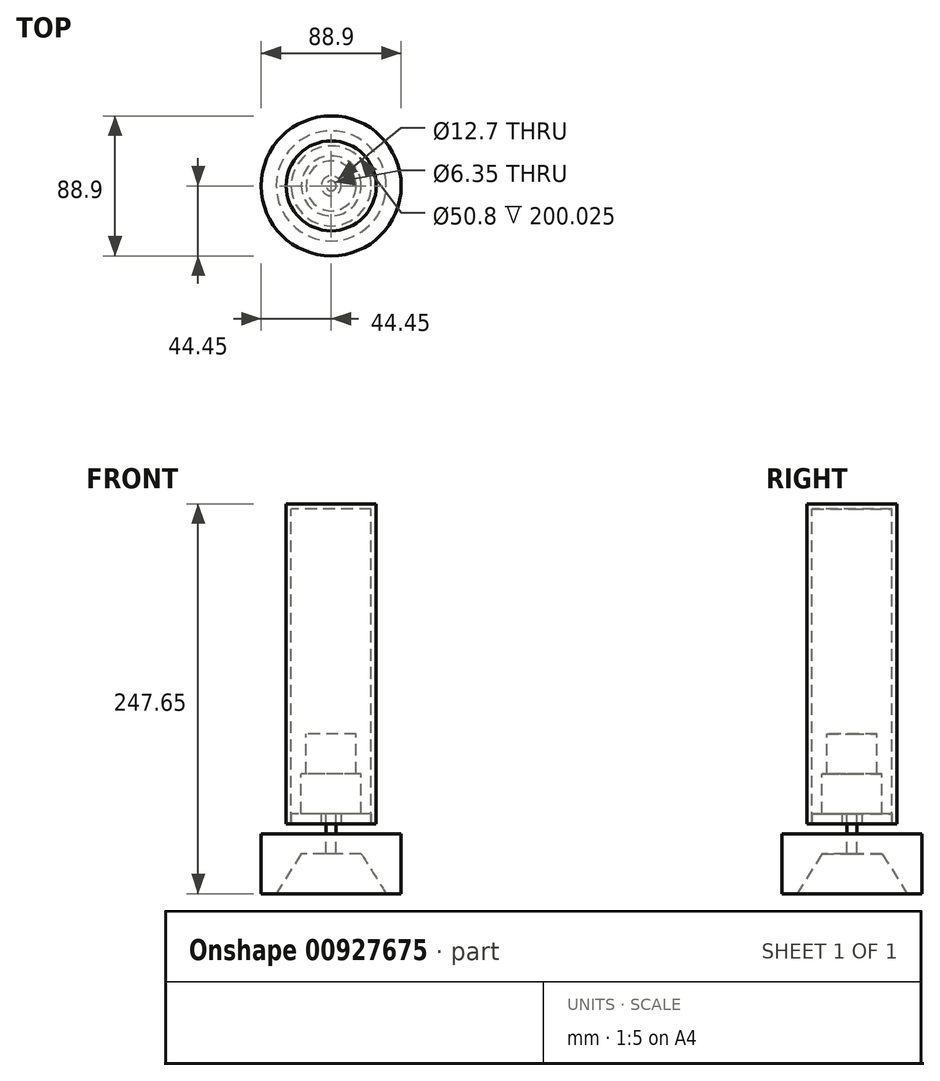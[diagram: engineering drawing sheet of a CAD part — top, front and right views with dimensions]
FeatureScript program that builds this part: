
annotation { "Feature Type Name" : "Feature", "Feature Type Description" : "" }
export const myFeature = defineFeature(function(context is Context, id is Id, definition is map)
    precondition{}
    {
        {
            var Q0;
            Q0=qCreatedBy(makeId("Front.planeOp"),FACE);
            var sketch = newSketch(context, id + "F0", { "sketchPlane" : qUnion([Q0])});
            skLineSegment(sketch, "E0", {"start": v(-25.4, 0) * mm, "end": v(-28.57, 0) * mm});
            skLineSegment(sketch, "E1", {"start": v(-28.57, 0) * mm, "end": v(-28.57, 203.2) * mm});
            skLineSegment(sketch, "E2", {"start": v(-28.57, 203.2) * mm, "end": v(0, 203.2) * mm});
            skLineSegment(sketch, "E3", {"start": v(0, 200.03) * mm, "end": v(-25.4, 200.03) * mm});
            skLineSegment(sketch, "E4", {"start": v(-25.4, 200.03) * mm, "end": v(-25.4, 0) * mm});
            skLineSegment(sketch, "E5", {"start": v(0, 200.03) * mm, "end": v(0, 203.2) * mm});
            skLineSegment(sketch, "E6", {"start": v(0, 200.03) * mm, "end": v(0, 0) * mm, "construction": true});
            skSolve(sketch);
        }
        {
            var Q0;
            Q0 = qSketchRegion(id + "F0", true);
            var Q1;
            Q1=sQuery(id+"F0.wireOp",EDGE,"E6");
            revolve(context, id + "F1", {"surfaceOperationType" : NewSurfaceOperationType.NEW, "entities" : qUnion([Q0]), "axis" : qUnion([Q1]), "revolveType" : RevolveType.FULL});
        }
        {
            var Q0;
            Q0=qCreatedBy(makeId("Top.planeOp"),FACE);
            var sketch = newSketch(context, id + "F2", { "sketchPlane" : qUnion([Q0])});
            skCircle(sketch, "E7", {"center": v(0, 0) * mm, "radius": 25.4 * mm});
            skCircle(sketch, "E8", {"center": v(0, 0) * mm, "radius": 6.35 * mm});
            skSolve(sketch);
        }
        {
            var Q0;
            Q0=makeQuery(id+"F2.imprint","IMPRINT",FACE,{"disambiguationData":[TD([[makeQuery(id+"F2.imprint","IMPRINT",EDGE,{"derivedFrom":sQuery(id+"F2.wireOp",EDGE,"E7")}),1.0]])]});
            extrude(context, id + "F3", {"entities" : qUnion([Q0]), "depth" : 6.35 * mm, "offsetDistance" : 25.4 * mm});
        }
        {
            var Q0;
            Q0=qCreatedBy(makeId("Front.planeOp"),FACE);
            var sketch = newSketch(context, id + "F4", { "sketchPlane" : qUnion([Q0])});
            skLineSegment(sketch, "E9", {"start": v(0, 6.35) * mm, "end": v(-19.05, 6.35) * mm});
            skLineSegment(sketch, "E10", {"start": v(-19.05, 6.35) * mm, "end": v(-19.05, 31.75) * mm});
            skLineSegment(sketch, "E11", {"start": v(-19.05, 31.75) * mm, "end": v(-15.87, 31.75) * mm});
            skLineSegment(sketch, "E12", {"start": v(-15.87, 31.75) * mm, "end": v(-15.88, 57.15) * mm});
            skLineSegment(sketch, "E13", {"start": v(-15.88, 57.15) * mm, "end": v(0, 57.15) * mm});
            skLineSegment(sketch, "E14", {"start": v(0, 57.15) * mm, "end": v(0, 6.35) * mm});
            skLineSegment(sketch, "E15", {"start": v(0, 6.35) * mm, "end": v(0, -19.05) * mm});
            skLineSegment(sketch, "E16", {"start": v(0, -19.05) * mm, "end": v(-3.18, -19.05) * mm});
            skLineSegment(sketch, "E17", {"start": v(-3.17, -19.05) * mm, "end": v(-3.17, 6.35) * mm});
            skSolve(sketch);
        }
        {
            var Q0;
            Q0=makeQuery(id+"F4.imprint","IMPRINT",FACE,{"disambiguationData":[TD([[makeQuery(id+"F4.imprint","IMPRINT",EDGE,{"derivedFrom":sQuery(id+"F4.wireOp",EDGE,"E9")}),-1.0]])]});
            var Q1;
            {var subQ0=sQuery(id+"F4.wireOp",EDGE,"E15");Q1=makeQuery(id+"F4.imprint","IMPRINT",FACE,{"disambiguationData":[TD([[makeQuery(id+"F4.imprint","IMPRINT",EDGE,{"derivedFrom":subQ0}),-1.0]])]});}
            var Q2;
            Q2=sQuery(id+"F4.wireOp",EDGE,"E14");
            revolve(context, id + "F5", {"surfaceOperationType" : NewSurfaceOperationType.NEW, "entities" : qUnion([Q0, Q1]), "axis" : qUnion([Q2]), "revolveType" : RevolveType.FULL});
        }
        {
            var Q0;
            Q0=qCreatedBy(makeId("Front.planeOp"),FACE);
            var sketch = newSketch(context, id + "F6", { "sketchPlane" : qUnion([Q0])});
            skLineSegment(sketch, "E18", {"start": v(3.17, -6.35) * mm, "end": v(44.45, -6.35) * mm});
            skLineSegment(sketch, "E19", {"start": v(44.45, -6.35) * mm, "end": v(44.45, -44.45) * mm});
            skLineSegment(sketch, "E20", {"start": v(44.45, -44.45) * mm, "end": v(34.93, -44.45) * mm});
            skLineSegment(sketch, "E21", {"start": v(34.93, -44.45) * mm, "end": v(19.05, -19.05) * mm});
            skLineSegment(sketch, "E22", {"start": v(19.05, -19.05) * mm, "end": v(3.17, -19.05) * mm});
            skLineSegment(sketch, "E23", {"start": v(3.17, -19.05) * mm, "end": v(3.17, -6.35) * mm});
            skLineSegment(sketch, "E24", {"start": v(0, -19.05) * mm, "end": v(0, -44.45) * mm, "construction": true});
            skSolve(sketch);
        }
        {
            var Q0;
            Q0=makeQuery(id+"F6.imprint","IMPRINT",FACE,{"disambiguationData":[TD([[makeQuery(id+"F6.imprint","IMPRINT",EDGE,{"derivedFrom":sQuery(id+"F6.wireOp",EDGE,"E18")}),-1.0]])]});
            var Q1;
            Q1=sQuery(id+"F6.wireOp",EDGE,"E24");
            revolve(context, id + "F7", {"surfaceOperationType" : NewSurfaceOperationType.NEW, "entities" : qUnion([Q0]), "axis" : qUnion([Q1]), "revolveType" : RevolveType.FULL});
        }
    });
